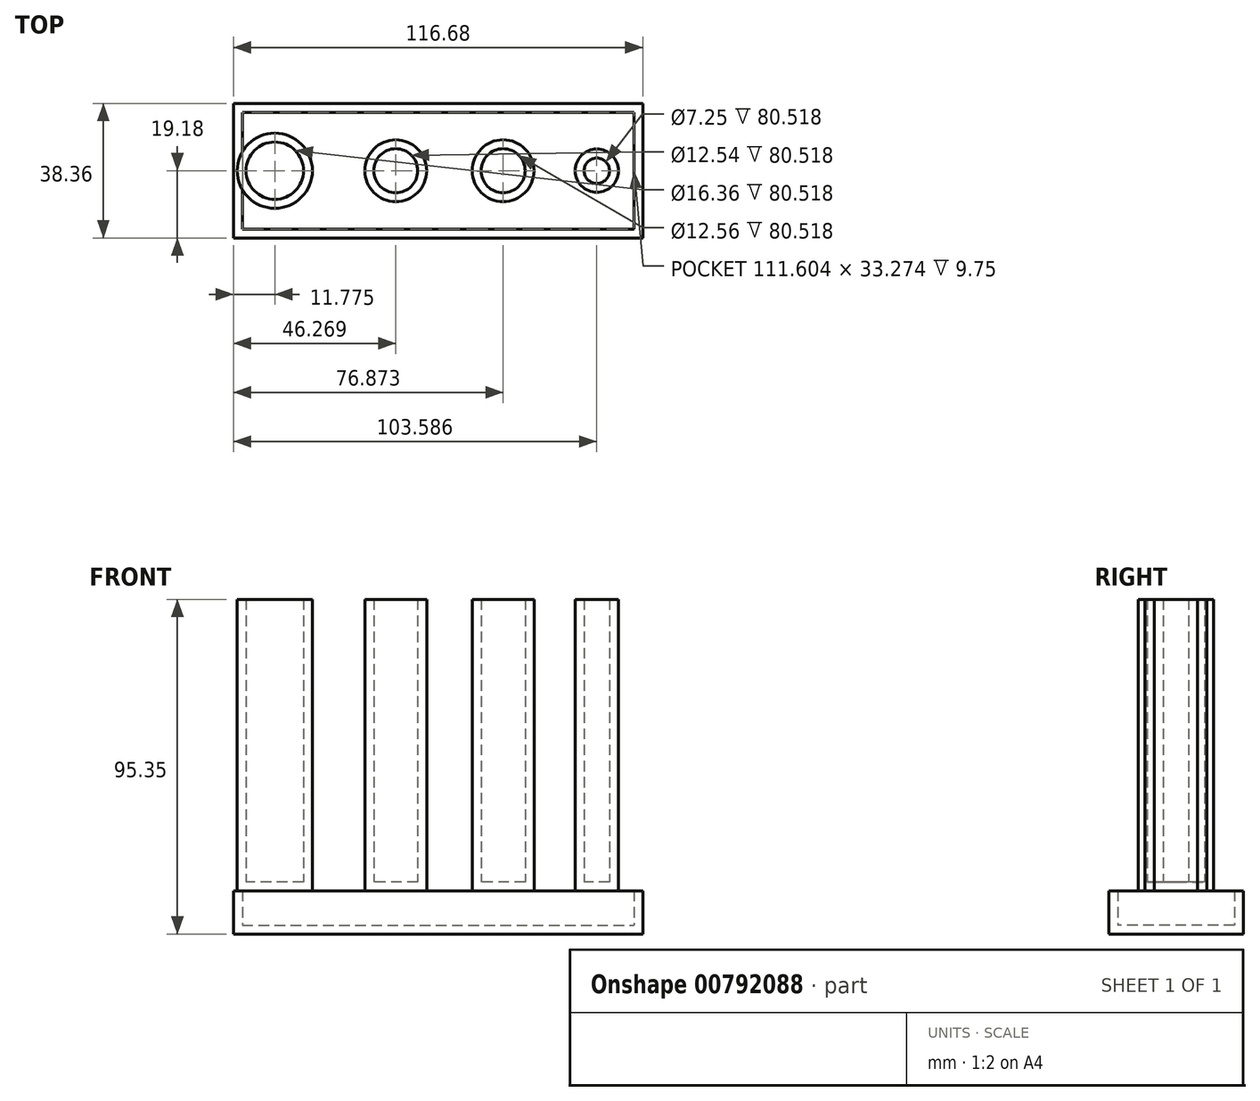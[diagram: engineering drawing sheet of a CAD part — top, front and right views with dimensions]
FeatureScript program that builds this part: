
annotation { "Feature Type Name" : "Feature", "Feature Type Description" : "" }
export const myFeature = defineFeature(function(context is Context, id is Id, definition is map)
    precondition{}
    {
        {
            var Q0;
            Q0=qCreatedBy(makeId("Top.planeOp"),FACE);
            var sketch = newSketch(context, id + "F0", { "sketchPlane" : qUnion([Q0])});
            skCircle(sketch, "E0", {"center": v(-50.18, 0) * mm, "radius": 10.72 * mm});
            skCircle(sketch, "E1", {"center": v(-15.7, 0) * mm, "radius": 8.81 * mm});
            skCircle(sketch, "E2", {"center": v(14.91, 0) * mm, "radius": 8.82 * mm});
            skCircle(sketch, "E3", {"center": v(41.63, 0) * mm, "radius": 6.16 * mm});
            skSolve(sketch);
        }
        {
            var Q0;
            Q0 = qSketchRegion(id + "F0", true);
            extrude(context, id + "F1", {"entities" : qUnion([Q0]), "depth" : 83.06 * mm, "offsetDistance" : 25.4 * mm});
        }
        {
            var Q0;
            Q0=qCreatedBy(makeId("Front.planeOp"),FACE);
            var sketch = newSketch(context, id + "F2", { "sketchPlane" : qUnion([Q0])});
            skLineSegment(sketch, "E4.bottom", {"start": v(-61.96, 0) * mm, "end": v(54.72, 0) * mm});
            skLineSegment(sketch, "E4.top", {"start": v(-61.96, -12.3) * mm, "end": v(54.72, -12.3) * mm});
            skLineSegment(sketch, "E4.left", {"start": v(-61.96, 0) * mm, "end": v(-61.96, -12.3) * mm});
            skLineSegment(sketch, "E4.right", {"start": v(54.72, 0) * mm, "end": v(54.72, -12.3) * mm});
            skSolve(sketch);
        }
        {
            var Q0;
            Q0 = qSketchRegion(id + "F2", true);
            extrude(context, id + "F3", {"entities" : qUnion([Q0]), "endBound" : BoundingType.SYMMETRIC, "oppositeDirection" : true, "depth" : 38.35 * mm, "offsetDistance" : 25.4 * mm});
        }
        {
            var Q0;
            Q0=makeQuery(id+"F1.opExtrude","CAP_FACE",FACE,{"disambiguationData":[OSD([sQuery(id+"F0.wireOp",EDGE,"E0")])],"isStart":false});
            var Q1;
            Q1=makeQuery(id+"F1.opExtrude","CAP_FACE",FACE,{"disambiguationData":[OSD([sQuery(id+"F0.wireOp",EDGE,"E2")])],"isStart":false});
            var Q2;
            Q2=makeQuery(id+"F1.opExtrude","CAP_FACE",FACE,{"disambiguationData":[OSD([sQuery(id+"F0.wireOp",EDGE,"E3")])],"isStart":false});
            var Q3;
            Q3=makeQuery(id+"F1.opExtrude","CAP_FACE",FACE,{"disambiguationData":[OSD([sQuery(id+"F0.wireOp",EDGE,"E1")])],"isStart":false});
            shell(context, id + "F4", {"entities" : qUnion([Q0, Q1, Q2, Q3]), "thickness" : 2.54 * mm});
        }
        {
            var Q0;
            Q0=makeQuery(id+"F6xQAXtnjQuXO3O_5.opExtrude","CAP_FACE",FACE,{"disambiguationData":[OSD([sQuery(id+"FucBbdVqdozWdhi_5.wireOp",EDGE,"lUHpBRsP-5iGS-rcBS-glqU-B6b2NMBY9zoO")])],"isStart":true});
            var Q1;
            Q1=makeQuery(id+"F3.opExtrude","SWEPT_FACE",FACE,{"disambiguationData":[OSD([sQuery(id+"F2.wireOp",EDGE,"E4.bottom")])]});
            shell(context, id + "F5", {"entities" : qUnion([Q0, Q1]), "thickness" : 2.54 * mm});
        }
    });
